# Revit family: Sanitary_Taps-Mixers_hansgrohe_71663XXX-Vernis-Blend-Shower-mixer-set-f
name_source: partatom
category: Plumbing Fixtures
revit_build: Autodesk Revit 2018 (Build: 20190510_1515(x64)
units: mm (PartAtom-declared; Revit-internal decimal feet)

## family parameters
Always vertical = No
Cut with Voids When Loaded = No
OmniClass Number = 23.31.11.00
OmniClass Title = Faucets
Part Type = Normal
Room Calculation Point = No
Round Connector Dimension = Use Diameter
Shared = No
Work Plane-Based = Yes

## types (2) — shared parameters
Always visible = Yes
BIMobject category = Taps & Mixers
Default Elevation = 1219.2 mm  [stored 4 ft]
Description = Vernis Blend Shower mixer set for concealed installation
Design country = Germany
EAN code = 4059625399859
Edition number = 1
GTIN code = https://4059625399859
IFC Classification = Valve
Installation instructions = https://www.hansgrohe.com
Manufacturer = Hansgrohe
Manufacturer country = Germany
Manufacturer name = hansgrohe
Model = 71663XXX
Product Guid = 5c859690-6fd7-46d5-83bd-cd4e529cec59
Product SKU = 71663XXX
Product data url = https://bimobject.com
Product family = Vernis Blend
Product group = Shower mixers
Product name = 71663XXX Vernis Blend Shower mixer set for concealed installation
Product url = https://www.hansgrohe.com
QR code = https://bimobject.com
URL = https://www.hansgrohe.com
Weight Net (Kg) = 1,2

## per-type parameters (varying)
| type | Material |
| 670 Matte Black | Hansgrohe - Metal - 670 Matte Black |
| 000 Chrome | Hansgrohe - Metal - 000 Chrome |

note: [stored X ft] marks values corroborated as IEEE doubles in the binary element streams (Revit-internal decimal feet)

## geometry (parser evidence)
native form markers: Blend x16, Sweep x2
no freeform markers — native parametric forms only
